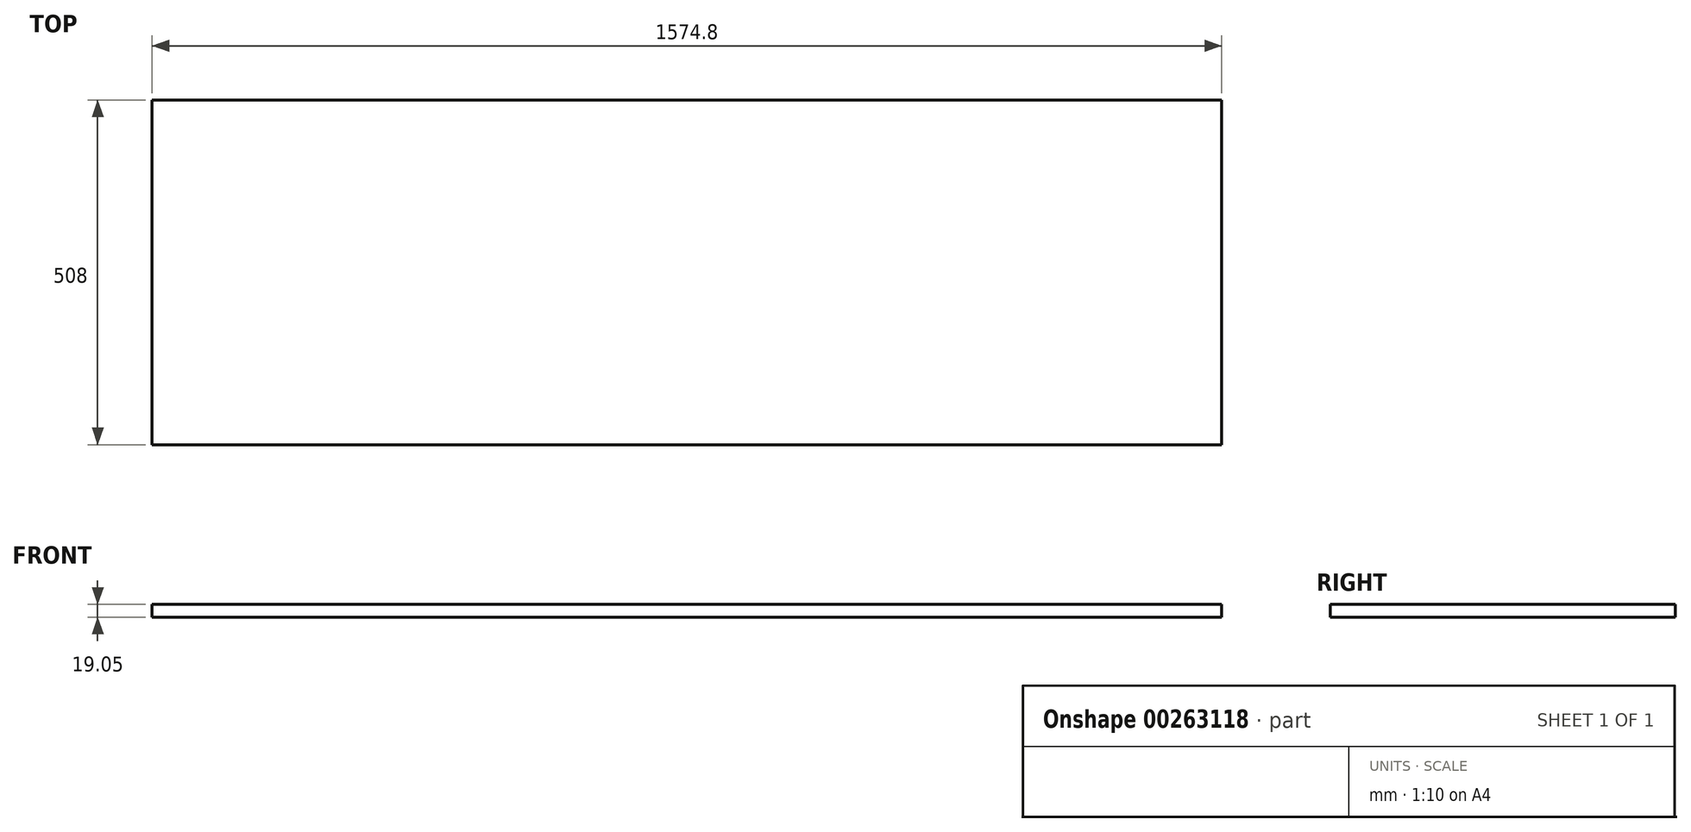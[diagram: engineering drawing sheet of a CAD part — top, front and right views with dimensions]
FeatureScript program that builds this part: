
annotation { "Feature Type Name" : "Feature", "Feature Type Description" : "" }
export const myFeature = defineFeature(function(context is Context, id is Id, definition is map)
    precondition{}
    {
        {
            var Q0;
            Q0=qCreatedBy(makeId("Top.planeOp"),FACE);
            var sketch = newSketch(context, id + "F0", { "sketchPlane" : qUnion([Q0])});
            skLineSegment(sketch, "E0.bottom", {"start": v(787.4, 254) * mm, "end": v(-787.4, 254) * mm});
            skLineSegment(sketch, "E0.top", {"start": v(787.4, -254) * mm, "end": v(-787.4, -254) * mm});
            skLineSegment(sketch, "E0.left", {"start": v(787.4, 254) * mm, "end": v(787.4, -254) * mm});
            skLineSegment(sketch, "E0.right", {"start": v(-787.4, 254) * mm, "end": v(-787.4, -254) * mm});
            skPoint(sketch, "E0.middle", {"position": v(0, 0) * mm});
            skSolve(sketch);
        }
        {
            var Q0;
            Q0 = qSketchRegion(id + "F0", true);
            extrude(context, id + "F1", {"entities" : qUnion([Q0]), "depth" : 19.05 * mm});
        }
    });
